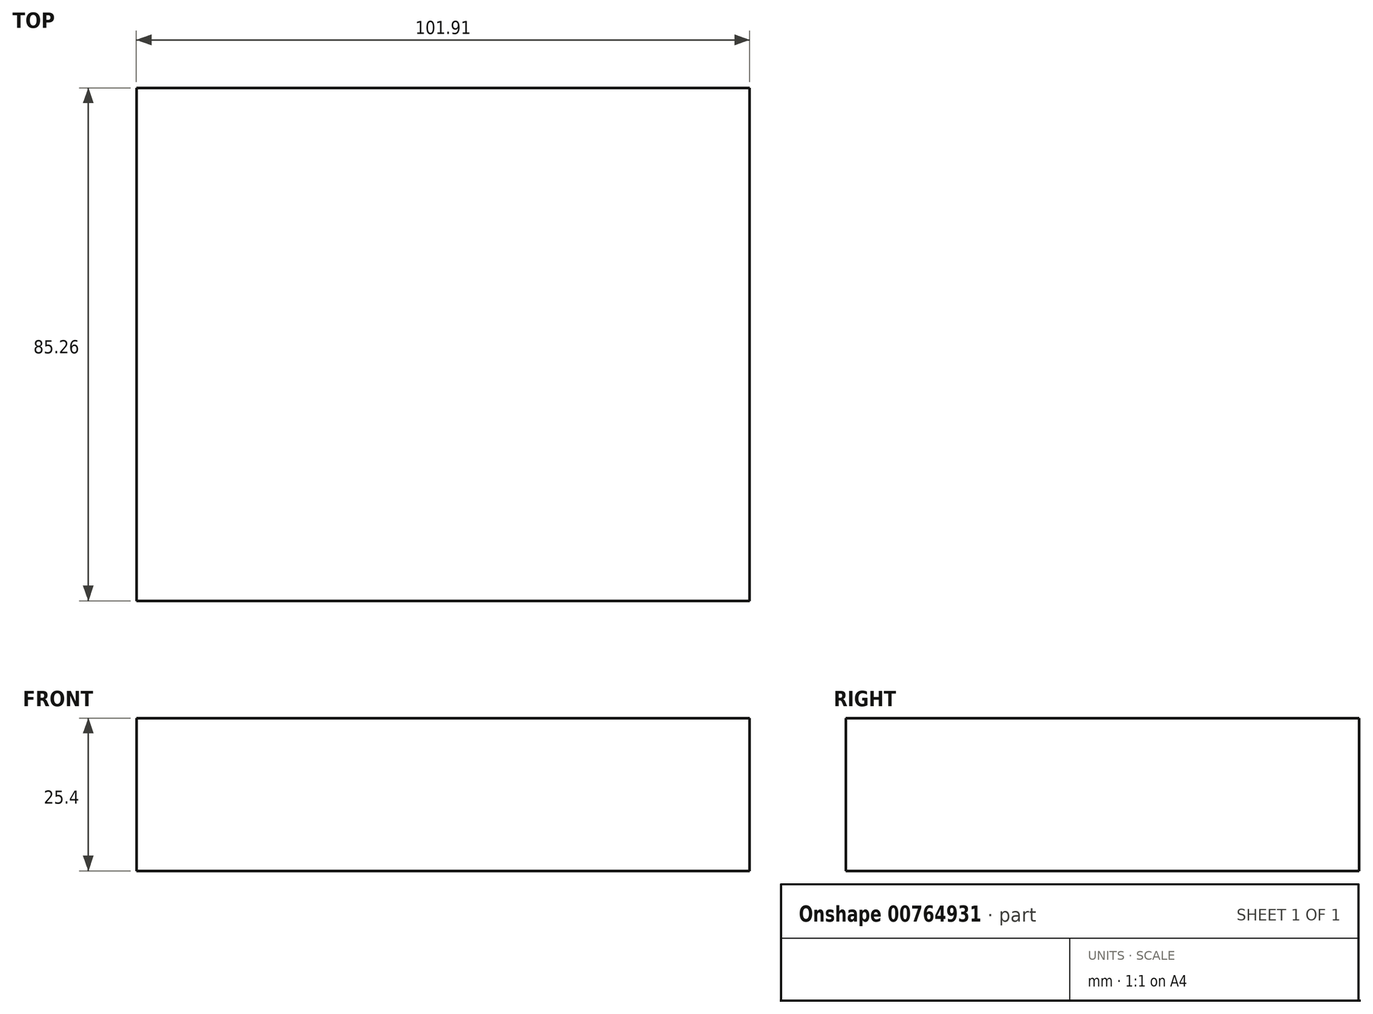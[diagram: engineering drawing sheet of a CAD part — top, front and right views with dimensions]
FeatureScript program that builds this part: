
annotation { "Feature Type Name" : "Feature", "Feature Type Description" : "" }
export const myFeature = defineFeature(function(context is Context, id is Id, definition is map)
    precondition{}
    {
        {
            var Q0;
            Q0=qCreatedBy(makeId("Top.planeOp"),FACE);
            var sketch = newSketch(context, id + "F0", { "sketchPlane" : qUnion([Q0])});
            skLineSegment(sketch, "E0", {"start": v(-51.25, 53.58) * mm, "end": v(50.66, 53.58) * mm});
            skLineSegment(sketch, "E1", {"start": v(50.66, -31.68) * mm, "end": v(50.66, 53.58) * mm});
            skLineSegment(sketch, "E2", {"start": v(50.66, -31.68) * mm, "end": v(-51.25, -31.68) * mm});
            skLineSegment(sketch, "E3", {"start": v(-51.25, 53.58) * mm, "end": v(-51.25, -31.68) * mm});
            skSolve(sketch);
        }
        {
            var Q0;
            Q0=makeQuery(id+"F0.imprint","IMPRINT",FACE,{"disambiguationData":[TD([[makeQuery(id+"F0.imprint","IMPRINT",EDGE,{"derivedFrom":sQuery(id+"F0.wireOp",EDGE,"E0")}),-1.0]])]});
            extrude(context, id + "F1", {"entities" : qUnion([Q0]), "depth" : 25.4 * mm, "offsetDistance" : 25.4 * mm});
        }
    });
